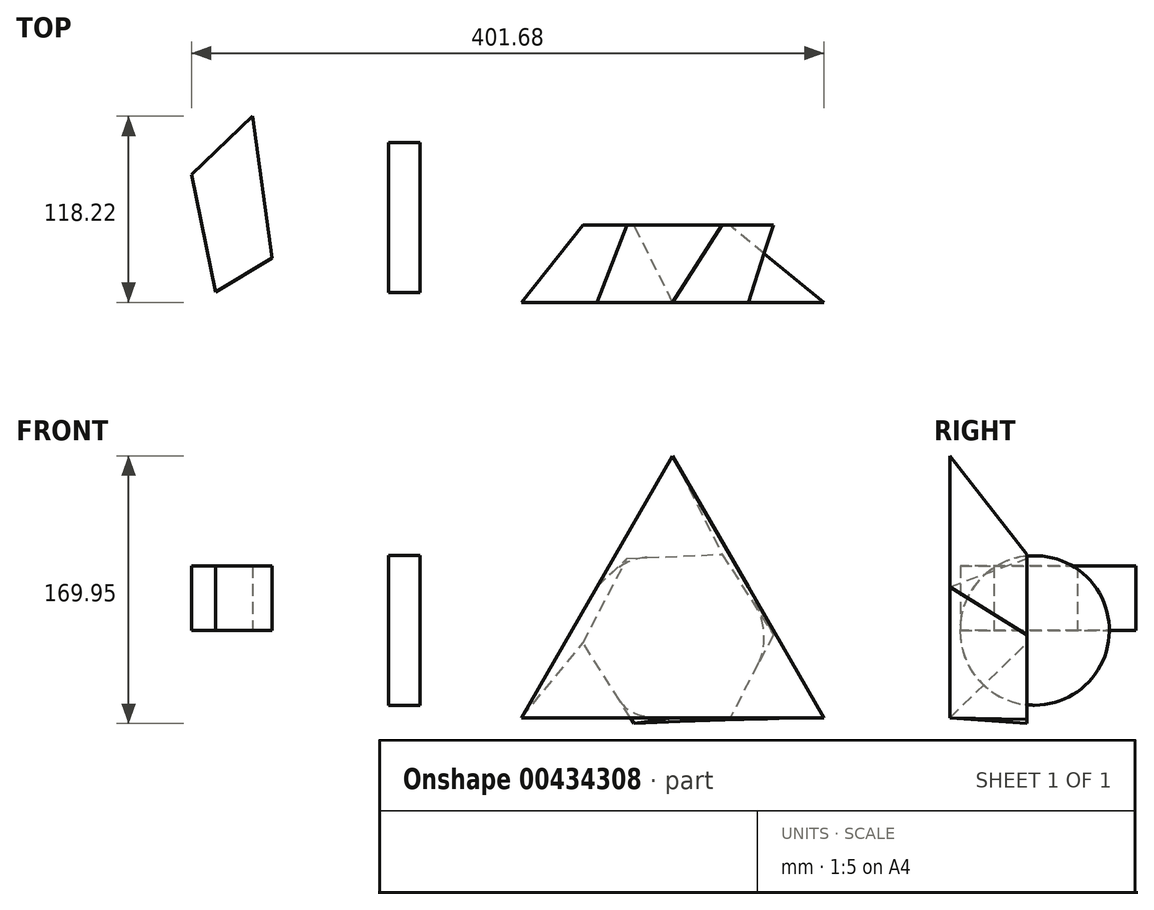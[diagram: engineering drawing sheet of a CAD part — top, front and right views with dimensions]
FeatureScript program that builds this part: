
annotation { "Feature Type Name" : "Feature", "Feature Type Description" : "" }
export const myFeature = defineFeature(function(context is Context, id is Id, definition is map)
    precondition{}
    {
        {
            var Q0;
            Q0=qCreatedBy(makeId("Top.planeOp"),FACE);
            var sketch = newSketch(context, id + "F0", { "sketchPlane" : qUnion([Q0])});
            skLineSegment(sketch, "E0", {"start": v(-125.04, 32.02) * mm, "end": v(-109.59, -42.35) * mm});
            skLineSegment(sketch, "E1", {"start": v(-109.59, -42.35) * mm, "end": v(-73.83, -20.93) * mm});
            skLineSegment(sketch, "E2", {"start": v(-73.83, -20.93) * mm, "end": v(-86.32, 69.22) * mm});
            skLineSegment(sketch, "E3", {"start": v(-86.32, 69.22) * mm, "end": v(-125.04, 32.02) * mm});
            skSolve(sketch);
        }
        {
            var Q0;
            Q0=makeQuery(id+"F0.imprint","IMPRINT",FACE,{"disambiguationData":[TD([[makeQuery(id+"F0.imprint","IMPRINT",EDGE,{"derivedFrom":sQuery(id+"F0.wireOp",EDGE,"E0")}),1.0]])]});
            extrude(context, id + "F1", {"entities" : qUnion([Q0]), "depth" : 41 * mm});
        }
        {
            var Q0;
            Q0=qCreatedBy(makeId("Right.planeOp"),FACE);
            var sketch = newSketch(context, id + "F2", { "sketchPlane" : qUnion([Q0])});
            skCircle(sketch, "E4", {"center": v(4.83, 0) * mm, "radius": 47.48 * mm});
            skSolve(sketch);
        }
        {
            var Q0;
            Q0=makeQuery(id+"F2.imprint","IMPRINT",FACE,{"disambiguationData":[TD([[makeQuery(id+"F2.imprint","IMPRINT",EDGE,{"derivedFrom":sQuery(id+"F2.wireOp",EDGE,"E4")}),1.0]])]});
            extrude(context, id + "F3", {"entities" : qUnion([Q0]), "depth" : 20 * mm});
        }
        {
            var Q0;
            Q0=qCreatedBy(makeId("Front.planeOp"),FACE);
            var sketch = newSketch(context, id + "F4", { "sketchPlane" : qUnion([Q0])});
            skCircle(sketch, "E5.cCircle", {"center": v(184.06, -5.33) * mm, "radius": 52.43 * mm, "construction": true});
            skLineSegment(sketch, "E5.0", {"start": v(156.07, -59) * mm, "end": v(123.58, -7.92) * mm});
            skLineSegment(sketch, "E5.1", {"start": v(123.58, -7.92) * mm, "end": v(151.57, 45.76) * mm});
            skLineSegment(sketch, "E5.2", {"start": v(151.57, 45.76) * mm, "end": v(212.06, 48.35) * mm});
            skLineSegment(sketch, "E5.3", {"start": v(212.06, 48.35) * mm, "end": v(244.55, -2.73) * mm});
            skLineSegment(sketch, "E5.4", {"start": v(244.55, -2.73) * mm, "end": v(216.56, -56.4) * mm});
            skLineSegment(sketch, "E5.5", {"start": v(216.56, -56.4) * mm, "end": v(156.07, -59) * mm});
            skPoint(sketch, "E5.0.midPoint", {"position": v(139.83, -33.47) * mm});
            skSolve(sketch);
        }
        {
            var Q0;
            Q0=makeQuery(id+"F4.imprint","IMPRINT",FACE,{"disambiguationData":[TD([[makeQuery(id+"F4.imprint","IMPRINT",EDGE,{"derivedFrom":sQuery(id+"F4.wireOp",EDGE,"E5.0")}),-1.0]])]});
            cPlane(context, id + "F5", {"entities" : qUnion([Q0]), "cplaneType" : CPlaneType.OFFSET, "offset" : 49 * mm, "width" : 150 * mm, "height" : 150 * mm});
        }
        {
            var Q0;
            Q0=qCreatedBy(id+"F5.planeOp",FACE);
            var sketch = newSketch(context, id + "F6", { "sketchPlane" : qUnion([Q0])});
            skCircle(sketch, "E6.cCircle", {"center": v(180.57, 0) * mm, "radius": 55.47 * mm, "construction": true});
            skLineSegment(sketch, "E6.0", {"start": v(276.64, -55.47) * mm, "end": v(84.49, -55.47) * mm});
            skLineSegment(sketch, "E6.1", {"start": v(84.49, -55.47) * mm, "end": v(180.57, 110.94) * mm});
            skLineSegment(sketch, "E6.2", {"start": v(180.57, 110.94) * mm, "end": v(276.64, -55.47) * mm});
            skPoint(sketch, "E6.0.midPoint", {"position": v(180.57, -55.47) * mm});
            skSolve(sketch);
        }
        {
            var Q0;
            Q0=makeQuery(id+"F6.imprint","IMPRINT",FACE,{"disambiguationData":[TD([[makeQuery(id+"F6.imprint","IMPRINT",EDGE,{"derivedFrom":sQuery(id+"F6.wireOp",EDGE,"E6.0")}),-1.0]])]});
            var Q1;
            Q1=makeQuery(id+"F4.imprint","IMPRINT",FACE,{"disambiguationData":[TD([[makeQuery(id+"F4.imprint","IMPRINT",EDGE,{"derivedFrom":sQuery(id+"F4.wireOp",EDGE,"E5.0")}),-1.0]])]});
            loft(context, id + "F7", {"sheetProfilesArray" : [{ "sheetProfileEntities" : qUnion([Q0]) }, { "sheetProfileEntities" : qUnion([Q1]) }]});
        }
    });
